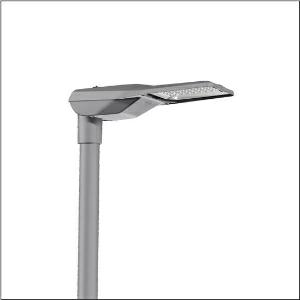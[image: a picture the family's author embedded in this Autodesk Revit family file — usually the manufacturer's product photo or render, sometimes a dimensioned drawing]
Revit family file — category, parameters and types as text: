
# Revit family: streetlight_sl_21_mini___st0_5a_5xe2b43s08jb_3299
name_source: partatom
category: Lighting Fixtures
units: mm (PartAtom-declared; Revit-internal decimal feet)

## family parameters
Cut with Voids When Loaded = No
Host = Face
Light Source = No
Part Type = Normal
Room Calculation Point = No
Round Connector Dimension = Use Diameter
Shared = No

## types (1)
- --- (1 x LED, 13390 lm, 87.3 W, 4000K)
    Apparent Load = 87 VA
    CIE Flux Codes = 43 76 97 100 100
    Color Rendering = 70
    Color Temperature = 4000K
    Default Elevation = 1800 mm
    Description = Streetlight SL 21 mini, mast luminaire, primary light control with lens, of PMMA, primary optical cover: cover, of toughened safety glass, transparent, light distribution: ST0.5a, light emission: direct distribution, primary light characteristic: asymmetric, installation type: side-entry, post-top, LED, High Power LED, rated luminous flux: 13.390lm, luminous efficacy: 153lm/W, light colour: 740, colour temperature: 4000K, control: overheat protection, constant luminous flux control, time-dependent luminous flux control, flexible luminous flux parameterisation, presetting dimming logarithmic, mains connection: 220..240V, AC, 50/60Hz, start of lifetime: 87W, end of service life: 90W, reduction: 40W, luminaire housing, of diecast aluminium, powder-coated, Siteco® metallic grey (DB 702S), corrosivity category C5 mid according to DIN EN ISO 12944, please order mast flange separately, inclination adjustable: 0°, 5°, 10°, 15°, sealing non-destructively replaceable, multi-level sealing system, length: 628mm, width: 235mm, height: 110mm, mast flange for spigot size: 42mm (side-entry): 5XC10008XM4, 60/48mm (side-entry/post-top): 5XC10108XM2, 76/60mm (side-entry/post-top): 5XC10108XM1, Smart Interface above, protection rating (complete): IP66, insulation class (complete): insulation class II (safety insulation), certification: CE, ENEC, ENEC+, VDE, impact resistance: IK09, permissible operating ambient temperature for outdoor applications: -40..+50°C, standard-compliant lighting for roads and squares, packaging unit: 1 piece

Light Distribution: ST0.5a
    Height = 110 mm
    Lamp = 1 x LED
    Lamp Light Flux = 13390 lm
    Lamp Power = 87.3 W
    Lamp count = 1
    Length = 625 mm
    Luminous efficacy = 153 lm/W
    Manufacturer = Siteco
    ModVariant = No
    Model = 5XE2B43S08JB
    Number of Poles = 1
    OnlyDefault = Yes
    Power Factor = 1
    Product Name = Streetlight SL 21 mini | ST0.5a
    Product group = mast luminaire | pylon top
    ProductGroupID = 6100
    Protection Class = Protection class II
    Protection Degree = IP 66
    RLX_Detail_Level = 1
    RLX_Emergency_Light_Flux = 0 lm
    RLX_Emergency_Type = 0
    RLX_Emergency_Type_DB = No
    RlxData = <blob elided: 103209 chars, md5=cc61ed91>
    Socket = socket
    Standby Power = 0 W
    System Light Flux = 13390 lm
    System Power = 87 W
    Type Comments = factory setting: luminous flux: 100 % | dim-lin: 254 | 915 mA
    Type Image = l_1003515.jpg
    URL = http://relux.com
    VarID = @adj_104701
    Voltage = 0 V
    Weight = 0.00 kg
    Width = 234 mm

## geometry (parser evidence)
native form markers: Blend x4, Sweep x11
no freeform markers — native parametric forms only
